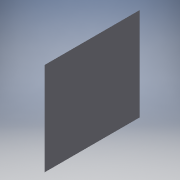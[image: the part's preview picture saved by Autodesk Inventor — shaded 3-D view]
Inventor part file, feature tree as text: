
AUTODESK INVENTOR PART (.ipt)
format: ipt  version: 2018 (Build 220112000, 112)  size: 129,024 bytes
history: native  units: mm
features: other x6, sketch x2, extrude x1, reference x1
ambient origin geometry x8: Origin, YZ Plane, XZ Plane, XY Plane, X Axis, Y Axis, Z Axis, Center Point
bodies: Volumenkörper1 (feature_tree)
feature tree (10):
  other  "Wand2.ipt"
  extrude  "Extrusion1"  Depth=90.0mm
  other  "Volumenkörper1::Wand2.ipt"
  other  "Bezeichnung1"
  sketch  "Skizze1"  dims[d0=10.0mm d1=90.0mm]
  sketch  "Skizze2"  dims[d2=50.0mm d3=30.0mm d4=4.0mm d5=15.0mm d6=0.0mm]
  reference  "Referenz1"
  parser-record x1  (decoder bookkeeping rows leaked as tree rows — omitted from the tree; the rows remain in map.json)
  other  "SmartCube_Quadratisch.iam"
  other  "PV_Ramen:1"
note: 1 file-system path scrubbed to <path> (originals preserved in map.json)
